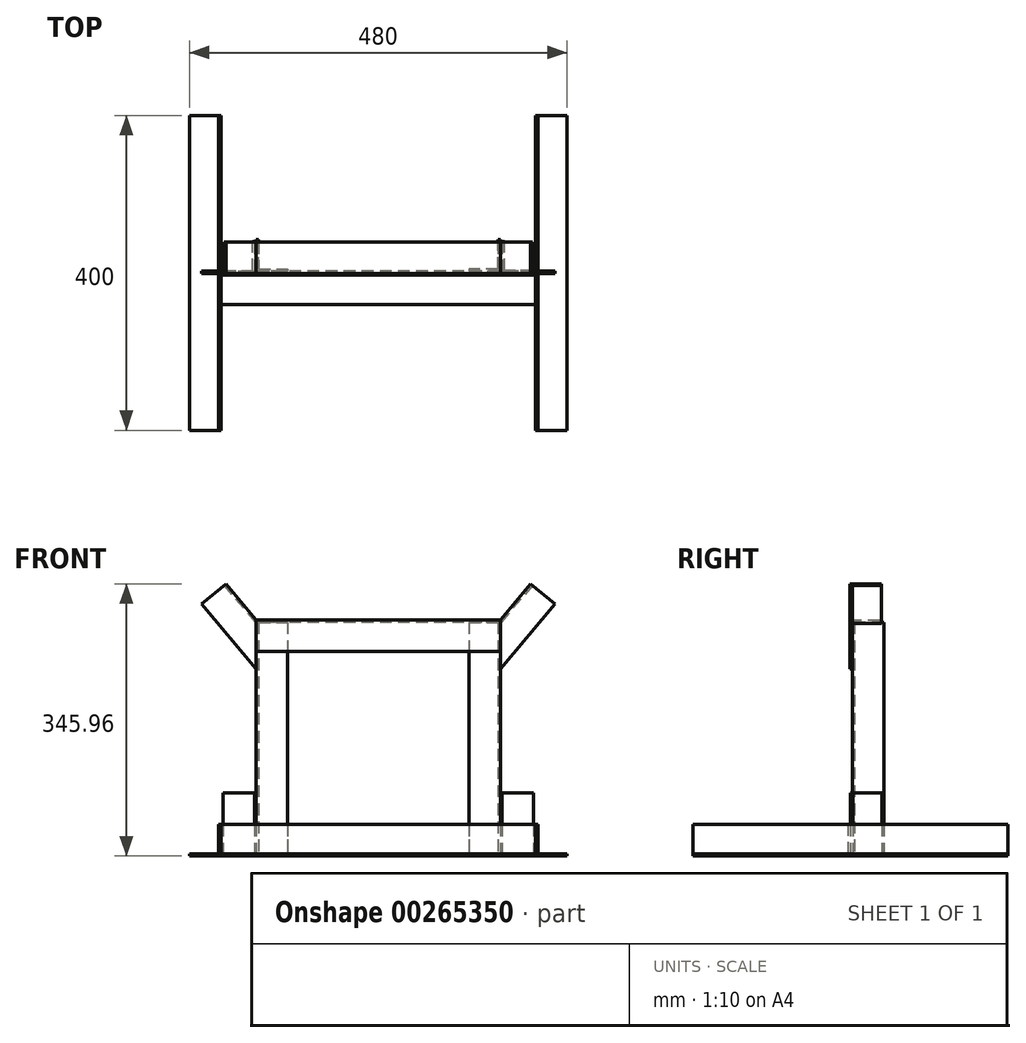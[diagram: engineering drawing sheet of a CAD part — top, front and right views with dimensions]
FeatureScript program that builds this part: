
annotation { "Feature Type Name" : "Feature", "Feature Type Description" : "" }
export const myFeature = defineFeature(function(context is Context, id is Id, definition is map)
    precondition{}
    {
        {
            var Q0;
            Q0=qCreatedBy(makeId("Right.planeOp"),FACE);
            var sketch = newSketch(context, id + "F0", { "sketchPlane" : qUnion([Q0])});
            skLineSegment(sketch, "E0", {"start": v(0, 40) * mm, "end": v(0, 0) * mm});
            skLineSegment(sketch, "E1", {"start": v(0, 0) * mm, "end": v(-40, 0) * mm});
            skLineSegment(sketch, "E2", {"start": v(-40, 0) * mm, "end": v(-40, 3) * mm});
            skLineSegment(sketch, "E3", {"start": v(-40, 3) * mm, "end": v(-3, 3) * mm});
            skLineSegment(sketch, "E4", {"start": v(-3, 3) * mm, "end": v(-3, 40) * mm});
            skLineSegment(sketch, "E5", {"start": v(-3, 40) * mm, "end": v(0, 40) * mm});
            skLineSegment(sketch, "E6", {"start": v(-1, 300) * mm, "end": v(39, 300) * mm});
            skLineSegment(sketch, "E7.MirrorCS", {"start": v(2, 260) * mm, "end": v(-1, 260) * mm});
            skLineSegment(sketch, "E8.MirrorCS", {"start": v(39, 300) * mm, "end": v(39, 297) * mm});
            skLineSegment(sketch, "E9.MirrorCS", {"start": v(2, 297) * mm, "end": v(2, 260) * mm});
            skLineSegment(sketch, "E10.MirrorCS", {"start": v(39, 297) * mm, "end": v(2, 297) * mm});
            skLineSegment(sketch, "E11.MirrorCS", {"start": v(-1, 260) * mm, "end": v(-1, 300) * mm});
            skSolve(sketch);
        }
        {
            var Q0;
            Q0=makeQuery(id+"F0.imprint","IMPRINT",FACE,{"disambiguationData":[TD([[makeQuery(id+"F0.imprint","IMPRINT",EDGE,{"derivedFrom":sQuery(id+"F0.wireOp",EDGE,"E6")}),-1.0]])]});
            extrude(context, id + "F1", {"entities" : qUnion([Q0]), "depth" : 155 * mm, "hasSecondDirection" : true, "secondDirectionOppositeDirection" : true, "secondDirectionDepth" : 155 * mm});
        }
        {
            var Q0;
            Q0=makeQuery(id+"F0.imprint","IMPRINT",FACE,{"disambiguationData":[TD([[makeQuery(id+"F0.imprint","IMPRINT",EDGE,{"derivedFrom":sQuery(id+"F0.wireOp",EDGE,"E0")}),-1.0]])]});
            extrude(context, id + "F2", {"entities" : qUnion([Q0]), "depth" : 200 * mm, "hasSecondDirection" : true, "secondDirectionOppositeDirection" : true, "secondDirectionDepth" : 200 * mm});
        }
        {
            var Q0;
            Q0=makeQuery(id+"F2.opExtrude","SWEPT_FACE",FACE,{"disambiguationData":[OSD([sQuery(id+"F0.wireOp",EDGE,"E1")])]});
            var sketch = newSketch(context, id + "F3", { "sketchPlane" : qUnion([Q0])});
            skLineSegment(sketch, "E12", {"start": v(155, -42) * mm, "end": v(155, -2) * mm});
            skLineSegment(sketch, "E13", {"start": v(155, -2) * mm, "end": v(115, -2) * mm});
            skLineSegment(sketch, "E14", {"start": v(115, -2) * mm, "end": v(115, -5) * mm});
            skLineSegment(sketch, "E15", {"start": v(115, -5) * mm, "end": v(152, -5) * mm});
            skPoint(sketch, "E15.endSnap0", {"position": v(152, -81.76) * mm});
            skLineSegment(sketch, "E16", {"start": v(152, -5) * mm, "end": v(152, -42) * mm});
            skLineSegment(sketch, "E17", {"start": v(152, -42) * mm, "end": v(155, -42) * mm});
            skLineSegment(sketch, "E18", {"start": v(0, 0) * mm, "end": v(0, -124.7) * mm, "construction": true});
            skLineSegment(sketch, "E19.MirrorCS", {"start": v(-152, -42) * mm, "end": v(-155, -42) * mm});
            skLineSegment(sketch, "E20.MirrorCS", {"start": v(-115, -2) * mm, "end": v(-115, -5) * mm});
            skLineSegment(sketch, "E21.MirrorCS", {"start": v(-155, -42) * mm, "end": v(-155, -2) * mm});
            skLineSegment(sketch, "E22.MirrorCS", {"start": v(-115, -5) * mm, "end": v(-152, -5) * mm});
            skLineSegment(sketch, "E23.MirrorCS", {"start": v(-155, -2) * mm, "end": v(-115, -2) * mm});
            skLineSegment(sketch, "E24.MirrorCS", {"start": v(-152, -5) * mm, "end": v(-152, -42) * mm});
            skSolve(sketch);
        }
        {
            var Q0;
            Q0=makeQuery(id+"F3.imprint","IMPRINT",FACE,{"disambiguationData":[TD([[makeQuery(id+"F3.imprint","IMPRINT",EDGE,{"derivedFrom":sQuery(id+"F3.wireOp",EDGE,"E12")}),1.0]])]});
            var Q1;
            Q1=makeQuery(id+"F3.imprint","IMPRINT",FACE,{"disambiguationData":[TD([[makeQuery(id+"F3.imprint","IMPRINT",EDGE,{"derivedFrom":sQuery(id+"F3.wireOp",EDGE,"E19.MirrorCS")}),-1.0]])]});
            var Q2;
            Q2=makeQuery(id+"F1.opExtrude","SWEPT_FACE",FACE,{"disambiguationData":[OSD([sQuery(id+"F0.wireOp",EDGE,"E10.MirrorCS")])]});
            var Q3;
            Q3=makeQuery(id+"F1.opExtrude","SWEPT_BODY",BODY,{"disambiguationData":[OSD([sQuery(id+"F0.wireOp",EDGE,"E6"),sQuery(id+"F0.wireOp",EDGE,"E7.MirrorCS"),sQuery(id+"F0.wireOp",EDGE,"E8.MirrorCS"),sQuery(id+"F0.wireOp",EDGE,"E9.MirrorCS"),sQuery(id+"F0.wireOp",EDGE,"E10.MirrorCS"),sQuery(id+"F0.wireOp",EDGE,"E11.MirrorCS")])]});
            extrude(context, id + "F4", {"entities" : qUnion([Q0, Q1]), "endBound" : BoundingType.UP_TO_SURFACE, "oppositeDirection" : true, "endBoundEntityFace" : qUnion([Q2]), "endBoundEntityBody" : qUnion([Q3]), "depth" : 25 * mm});
        }
        {
            var Q0;
            Q0=makeQuery(id+"F1.opExtrude","CAP_EDGE",EDGE,{"disambiguationData":[OSD([sQuery(id+"F0.wireOp",EDGE,"E6")])],"isStart":true});
            cPlane(context, id + "F5", {"entities" : qUnion([Q0]), "cplaneType" : CPlaneType.LINE_ANGLE, "offset" : 25 * mm, "angle" : 140 * degree, "width" : 150 * mm, "height" : 150 * mm});
        }
        {
            var Q0;
            Q0=qCreatedBy(id+"F5.planeOp",FACE);
            var sketch = newSketch(context, id + "F6", { "sketchPlane" : qUnion([Q0])});
            skLineSegment(sketch, "E25.0", {"start": v(74.1, 1) * mm, "end": v(74.1, -39) * mm});
            skLineSegment(sketch, "E26", {"start": v(74.1, -39) * mm, "end": v(71.1, -39) * mm});
            skLineSegment(sketch, "E27", {"start": v(71.1, -39) * mm, "end": v(71.1, -2) * mm});
            skLineSegment(sketch, "E28", {"start": v(71.1, -2) * mm, "end": v(34.1, -2) * mm});
            skLineSegment(sketch, "E29", {"start": v(34.1, -2) * mm, "end": v(34.1, 1) * mm});
            skLineSegment(sketch, "E30", {"start": v(34.1, 1) * mm, "end": v(74.1, 1) * mm});
            skSolve(sketch);
        }
        {
            var Q0;
            Q0=makeQuery(id+"F6.imprint","IMPRINT",FACE,{"disambiguationData":[TD([[makeQuery(id+"F6.imprint","IMPRINT",EDGE,{"derivedFrom":sQuery(id+"F6.wireOp",EDGE,"E25.0")}),-1.0]])]});
            var Q1;
            Q1=makeQuery(id+"F1.opExtrude","CAP_FACE",FACE,{"disambiguationData":[OSD([sQuery(id+"F0.wireOp",EDGE,"E6"),sQuery(id+"F0.wireOp",EDGE,"E7.MirrorCS"),sQuery(id+"F0.wireOp",EDGE,"E8.MirrorCS"),sQuery(id+"F0.wireOp",EDGE,"E9.MirrorCS"),sQuery(id+"F0.wireOp",EDGE,"E10.MirrorCS"),sQuery(id+"F0.wireOp",EDGE,"E11.MirrorCS")])],"isStart":true});
            var Q2;
            Q2=makeQuery(id+"F4.opExtrude","SWEPT_BODY",BODY,{"disambiguationData":[OSD([sQuery(id+"F3.wireOp",EDGE,"E19.MirrorCS"),sQuery(id+"F3.wireOp",EDGE,"E20.MirrorCS"),sQuery(id+"F3.wireOp",EDGE,"E21.MirrorCS"),sQuery(id+"F3.wireOp",EDGE,"E22.MirrorCS"),sQuery(id+"F3.wireOp",EDGE,"E23.MirrorCS"),sQuery(id+"F3.wireOp",EDGE,"E24.MirrorCS")])]});
            extrude(context, id + "F7", {"entities" : qUnion([Q0]), "oppositeDirection" : true, "depth" : 60 * mm, "hasSecondDirection" : true, "secondDirectionBound" : SecondDirectionBoundingType.UP_TO_SURFACE, "secondDirectionOppositeDirection" : false, "secondDirectionBoundEntityFace" : qUnion([Q1]), "secondDirectionBoundEntityBody" : qUnion([Q2]), "secondDirectionDepth" : 25 * mm});
        }
        {
            var Q0;
            Q0=makeQuery(id+"F7.opExtrude","SWEPT_BODY",BODY,{"disambiguationData":[OSD([sQuery(id+"F6.wireOp",EDGE,"E25.0"),sQuery(id+"F6.wireOp",EDGE,"E26"),sQuery(id+"F6.wireOp",EDGE,"E27"),sQuery(id+"F6.wireOp",EDGE,"E28"),sQuery(id+"F6.wireOp",EDGE,"E29"),sQuery(id+"F6.wireOp",EDGE,"E30")])]});
            var Q1;
            Q1=qCreatedBy(makeId("Right.planeOp"),FACE);
            mirror(context, id + "F8", {"entities" : qUnion([Q0]), "mirrorPlane" : qUnion([Q1])});
        }
        {
            var Q0;
            Q0=qCreatedBy(makeId("Front.planeOp"),FACE);
            var sketch = newSketch(context, id + "F9", { "sketchPlane" : qUnion([Q0])});
            skLineSegment(sketch, "E31", {"start": v(200, 0) * mm, "end": v(200, 40) * mm});
            skLineSegment(sketch, "E32", {"start": v(200, 40) * mm, "end": v(203, 40) * mm});
            skLineSegment(sketch, "E33", {"start": v(203, 40) * mm, "end": v(203, 3) * mm});
            skLineSegment(sketch, "E34", {"start": v(203, 3) * mm, "end": v(240, 3) * mm});
            skLineSegment(sketch, "E35", {"start": v(240, 3) * mm, "end": v(240, 0) * mm});
            skLineSegment(sketch, "E36", {"start": v(240, 0) * mm, "end": v(200, 0) * mm});
            skSolve(sketch);
        }
        {
            var Q0;
            Q0=makeQuery(id+"F9.imprint","IMPRINT",FACE,{"disambiguationData":[TD([[makeQuery(id+"F9.imprint","IMPRINT",EDGE,{"derivedFrom":sQuery(id+"F9.wireOp",EDGE,"E31")}),-1.0]])]});
            extrude(context, id + "F10", {"entities" : qUnion([Q0]), "depth" : 200 * mm, "hasSecondDirection" : true, "secondDirectionOppositeDirection" : true, "secondDirectionDepth" : 200 * mm});
        }
        {
            var Q0;
            Q0=makeQuery(id+"F10.opExtrude","SWEPT_BODY",BODY,{"disambiguationData":[OSD([sQuery(id+"F9.wireOp",EDGE,"E31"),sQuery(id+"F9.wireOp",EDGE,"E32"),sQuery(id+"F9.wireOp",EDGE,"E33"),sQuery(id+"F9.wireOp",EDGE,"E34"),sQuery(id+"F9.wireOp",EDGE,"E35"),sQuery(id+"F9.wireOp",EDGE,"E36")])]});
            var Q1;
            Q1=qCreatedBy(makeId("Right.planeOp"),FACE);
            mirror(context, id + "F11", {"entities" : qUnion([Q0]), "mirrorPlane" : qUnion([Q1])});
        }
        {
            var Q0;
            Q0=qCreatedBy(makeId("Top.planeOp"),FACE);
            var sketch = newSketch(context, id + "F12", { "sketchPlane" : qUnion([Q0])});
            skLineSegment(sketch, "E37", {"start": v(157, 40) * mm, "end": v(157, 0) * mm});
            skLineSegment(sketch, "E38", {"start": v(157, 0) * mm, "end": v(197, 0) * mm});
            skLineSegment(sketch, "E39", {"start": v(197, 0) * mm, "end": v(197, 3) * mm});
            skLineSegment(sketch, "E40", {"start": v(197, 3) * mm, "end": v(160, 3) * mm});
            skLineSegment(sketch, "E41", {"start": v(160, 3) * mm, "end": v(160, 40) * mm});
            skLineSegment(sketch, "E42", {"start": v(160, 40) * mm, "end": v(157, 40) * mm});
            skSolve(sketch);
        }
        {
            var Q0;
            Q0=makeQuery(id+"F12.imprint","IMPRINT",FACE,{"disambiguationData":[TD([[makeQuery(id+"F12.imprint","IMPRINT",EDGE,{"derivedFrom":sQuery(id+"F12.wireOp",EDGE,"E37")}),1.0]])]});
            extrude(context, id + "F13", {"entities" : qUnion([Q0]), "depth" : 80 * mm});
        }
        {
            var Q0;
            Q0=makeQuery(id+"F13.opExtrude","SWEPT_BODY",BODY,{"disambiguationData":[OSD([sQuery(id+"F12.wireOp",EDGE,"E37"),sQuery(id+"F12.wireOp",EDGE,"E38"),sQuery(id+"F12.wireOp",EDGE,"E39"),sQuery(id+"F12.wireOp",EDGE,"E40"),sQuery(id+"F12.wireOp",EDGE,"E41"),sQuery(id+"F12.wireOp",EDGE,"E42")])]});
            var Q1;
            Q1=qCreatedBy(makeId("Right.planeOp"),FACE);
            mirror(context, id + "F14", {"entities" : qUnion([Q0]), "mirrorPlane" : qUnion([Q1])});
        }
    });
